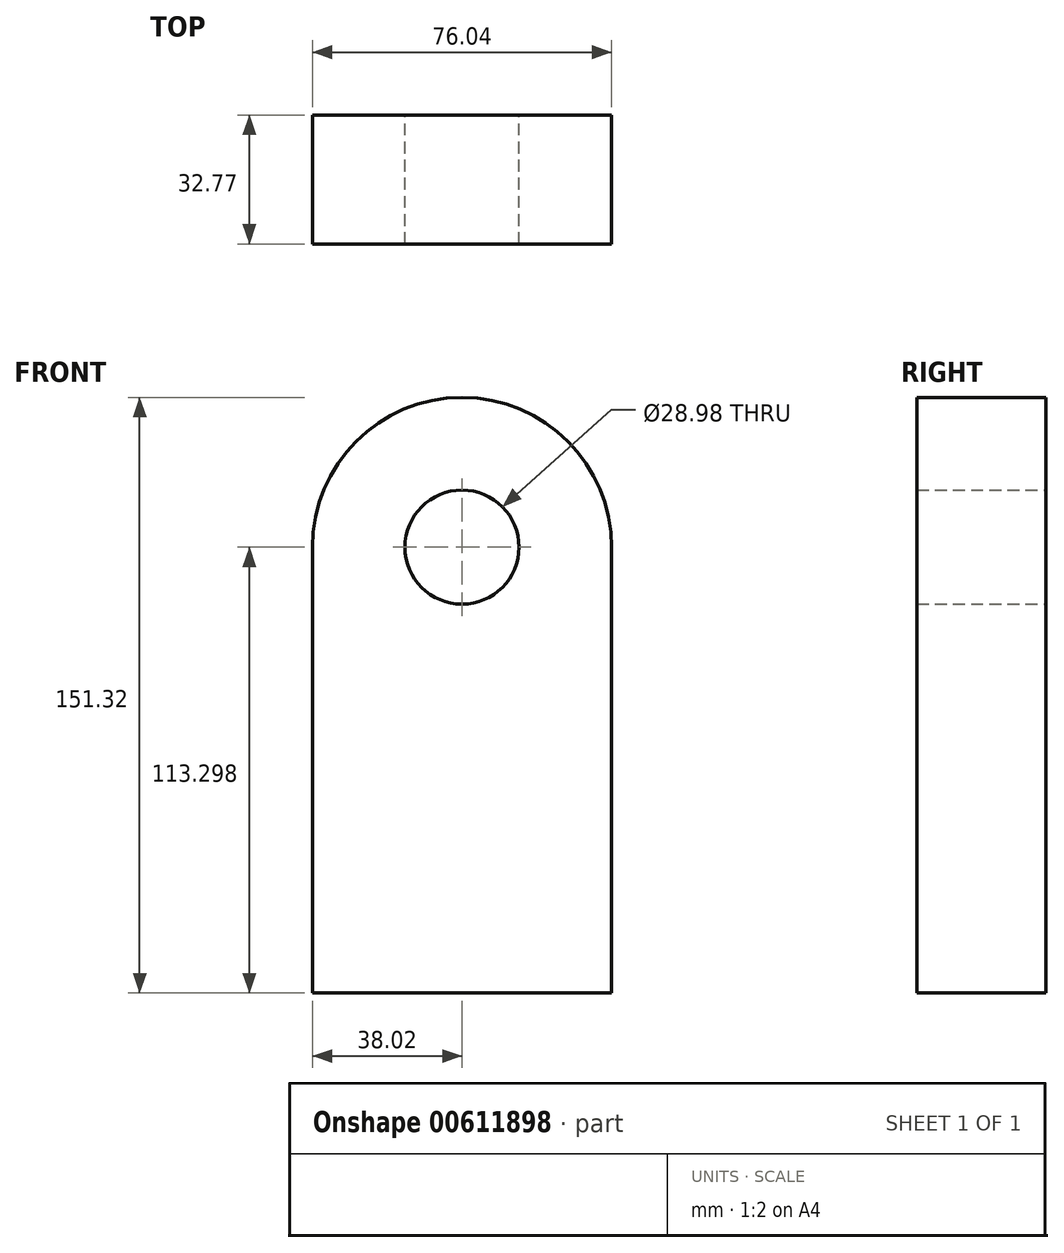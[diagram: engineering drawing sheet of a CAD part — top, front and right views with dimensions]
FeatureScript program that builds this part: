
annotation { "Feature Type Name" : "Feature", "Feature Type Description" : "" }
export const myFeature = defineFeature(function(context is Context, id is Id, definition is map)
    precondition{}
    {
        {
            var Q0;
            Q0=qCreatedBy(makeId("Front.planeOp"),FACE);
            var sketch = newSketch(context, id + "F0", { "sketchPlane" : qUnion([Q0])});
            skLineSegment(sketch, "E0.bottom", {"start": v(38.02, -56.65) * mm, "end": v(-38.02, -56.65) * mm});
            skLineSegment(sketch, "E0.left", {"start": v(38.02, -56.65) * mm, "end": v(38.02, 56.65) * mm});
            skLineSegment(sketch, "E0.right", {"start": v(-38.02, -56.65) * mm, "end": v(-38.02, 56.65) * mm});
            skPoint(sketch, "E0.middle", {"position": v(0, 0) * mm});
            skArc(sketch, "E1", {"start": v(38.02, 56.65) * mm, "mid": v(0, 94.67) * mm, "end": v(-38.02, 56.65) * mm});
            skCircle(sketch, "E2", {"center": v(0, 56.65) * mm, "radius": 14.49 * mm});
            skSolve(sketch);
        }
        {
            var Q0;
            Q0=makeQuery(id+"F0.imprint","IMPRINT",FACE,{"disambiguationData":[TD([[makeQuery(id+"F0.imprint","IMPRINT",EDGE,{"derivedFrom":sQuery(id+"F0.wireOp",EDGE,"E0.bottom")}),-1.0]])]});
            extrude(context, id + "F1", {"entities" : qUnion([Q0]), "depth" : 32.77 * mm, "offsetDistance" : 25.4 * mm});
        }
    });
